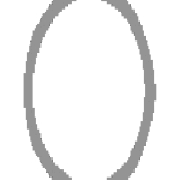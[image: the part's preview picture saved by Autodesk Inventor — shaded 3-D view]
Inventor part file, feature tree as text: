
AUTODESK INVENTOR PART (.ipt)
format: ipt  version: 2021 (Build 250183000, 183)  size: 110,080 bytes
history: native  units: in
note: dims shown in document units (in); Inventor stores cm internally (conversion verified against a paired STEP export)
features: other x4, sketch x3, plane x1
ambient origin geometry x8: Origin, YZ Plane, XZ Plane, XY Plane, X Axis, Y Axis, Z Axis, Center Point
bodies: Solid1 (feature_tree), Body (feature_tree)
feature tree (8):
  other  "Driven Length"
  other  "Frame Generator"
  other  "Start Plane"
  other  "End Plane"
  sketch  "Sketch"  dims[d2=18.6078in d4=-0.0in d5=18.6078in d6=0.12in d7=0.0in d8=90.0deg d9=18.6078in]
  sketch  "Sketch2"  dims[d0=1.0in]
  plane  "Work Plane3"
  sketch  "Sketch3"  dims[d1=0.065in]
